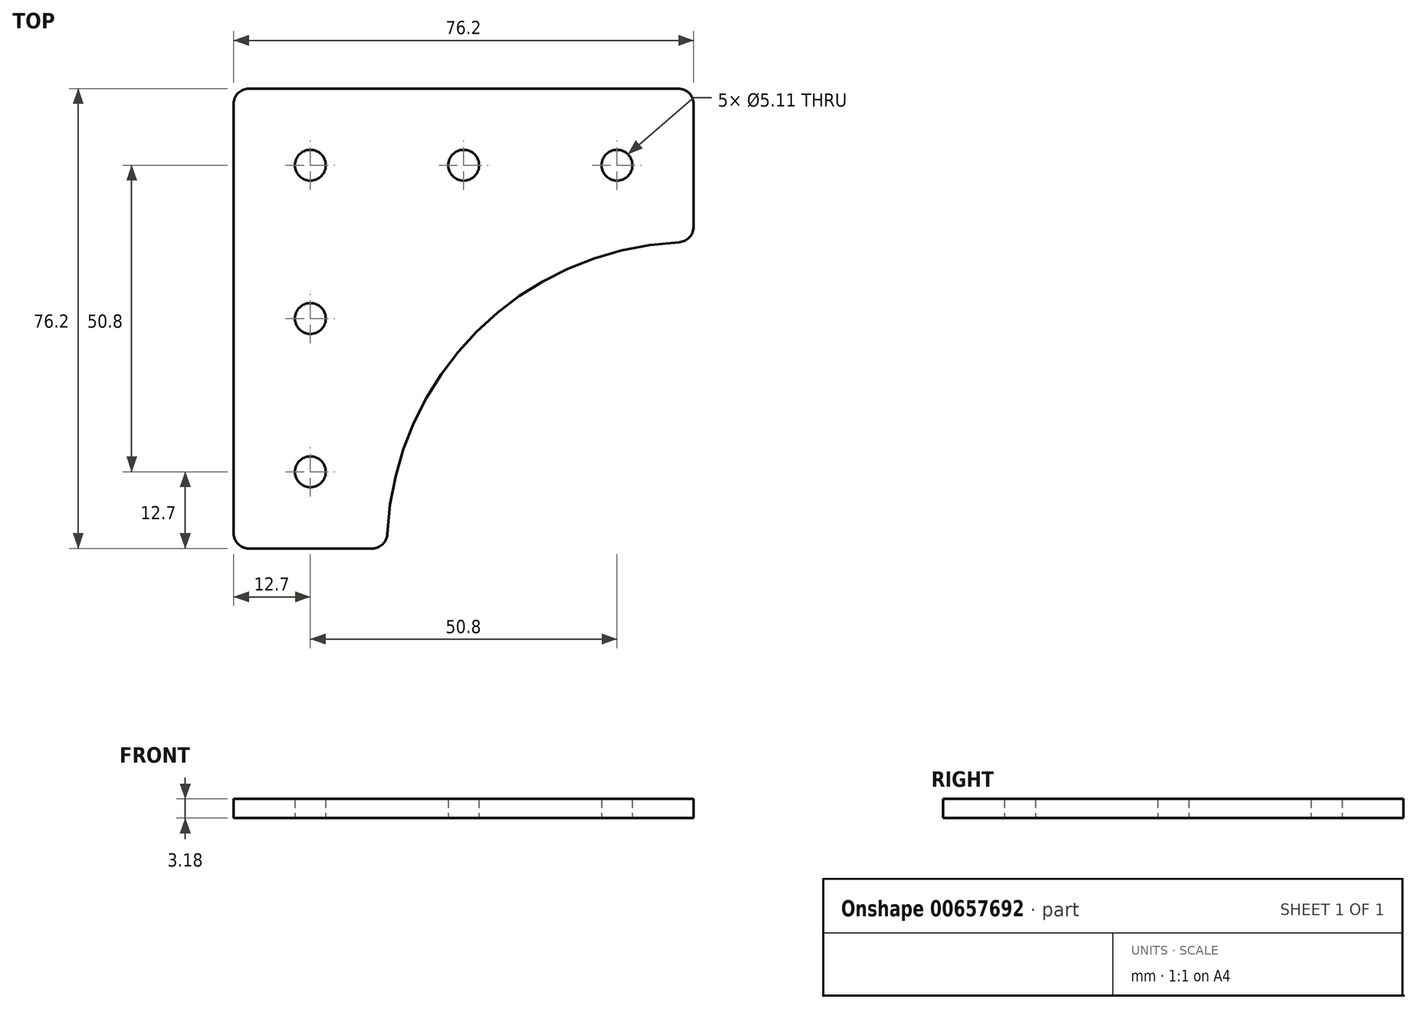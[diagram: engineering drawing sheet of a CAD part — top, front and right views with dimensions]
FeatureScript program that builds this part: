
annotation { "Feature Type Name" : "Feature", "Feature Type Description" : "" }
export const myFeature = defineFeature(function(context is Context, id is Id, definition is map)
    precondition{}
    {
        {
            var Q0;
            Q0=qCreatedBy(makeId("Top.planeOp"),FACE);
            var sketch = newSketch(context, id + "F0", { "sketchPlane" : qUnion([Q0])});
            skLineSegment(sketch, "E0.bottom", {"start": v(0, 0) * mm, "end": v(76.2, 0) * mm});
            skLineSegment(sketch, "E0.top", {"start": v(0, -76.2) * mm, "end": v(76.2, -76.2) * mm});
            skLineSegment(sketch, "E0.left", {"start": v(0, 0) * mm, "end": v(0, -76.2) * mm});
            skLineSegment(sketch, "E0.right", {"start": v(76.2, 0) * mm, "end": v(76.2, -76.2) * mm});
            skLineSegment(sketch, "E1", {"start": v(38.1, -76.2) * mm, "end": v(76.2, -38.1) * mm});
            skLineSegment(sketch, "E2", {"start": v(12.7, -76.2) * mm, "end": v(12.7, 0) * mm});
            skLineSegment(sketch, "E3", {"start": v(0, -12.7) * mm, "end": v(76.2, -12.7) * mm});
            skCircle(sketch, "E4", {"center": v(12.7, -12.7) * mm, "radius": 2.55 * mm});
            skCircle(sketch, "E5", {"center": v(38.1, -12.7) * mm, "radius": 2.55 * mm});
            skCircle(sketch, "E6", {"center": v(63.5, -12.7) * mm, "radius": 2.55 * mm});
            skCircle(sketch, "E7", {"center": v(12.7, -38.1) * mm, "radius": 2.55 * mm});
            skCircle(sketch, "E8", {"center": v(12.7, -63.5) * mm, "radius": 2.55 * mm});
            skLineSegment(sketch, "E9.bottom", {"start": v(76.2, -76.2) * mm, "end": v(25.4, -76.2) * mm});
            skLineSegment(sketch, "E9.top", {"start": v(76.2, -25.4) * mm, "end": v(25.4, -25.4) * mm});
            skLineSegment(sketch, "E9.left", {"start": v(76.2, -76.2) * mm, "end": v(76.2, -25.4) * mm});
            skLineSegment(sketch, "E9.right", {"start": v(25.4, -76.2) * mm, "end": v(25.4, -25.4) * mm});
            skSolve(sketch);
        }
        {
            var Q0;
            {var subQ5=sQuery(id+"F0.wireOp",EDGE,"E0.left");var subQ6=sQuery(id+"F0.wireOp",EDGE,"E0.top");var subQ7=makeQuery(id+"F0.imprint","INTERSECT",VERTEX,{"derivedFrom":[subQ6,subQ5]});Q0=makeQuery(id+"F0.imprint","IMPRINT",FACE,{"disambiguationData":[TD([[makeQuery(id+"F0.imprint","IMPRINT",EDGE,{"disambiguationData":[TD([[subQ7,-1.0]])],"derivedFrom":subQ6}),1.0]])]});}
            var Q1;
            {var subQ1=sQuery(id+"F0.wireOp",EDGE,"E0.left");var subQ6=sQuery(id+"F0.wireOp",EDGE,"E0.bottom");var subQ9=makeQuery(id+"F0.imprint","INTERSECT",VERTEX,{"derivedFrom":[subQ6,subQ1]});Q1=makeQuery(id+"F0.imprint","IMPRINT",FACE,{"disambiguationData":[TD([[makeQuery(id+"F0.imprint","IMPRINT",EDGE,{"disambiguationData":[TD([[subQ9,-1.0]])],"derivedFrom":subQ6}),-1.0]])]});}
            var Q2;
            {var subQ1=sQuery(id+"F0.wireOp",EDGE,"E0.bottom");var subQ5=sQuery(id+"F0.wireOp",EDGE,"E0.right");var subQ6=makeQuery(id+"F0.imprint","INTERSECT",VERTEX,{"derivedFrom":[subQ1,subQ5]});Q2=makeQuery(id+"F0.imprint","IMPRINT",FACE,{"disambiguationData":[TD([[makeQuery(id+"F0.imprint","IMPRINT",EDGE,{"disambiguationData":[TD([[subQ6,1.0]])],"derivedFrom":subQ1}),-1.0]])]});}
            var Q3;
            {var subQ4=sQuery(id+"F0.wireOp",EDGE,"E9.top");Q3=makeQuery(id+"F0.imprint","IMPRINT",FACE,{"disambiguationData":[TD([[makeQuery(id+"F0.imprint","IMPRINT",EDGE,{"derivedFrom":subQ4}),-1.0]])]});}
            extrude(context, id + "F1", {"entities" : qUnion([Q0, Q1, Q2, Q3]), "depth" : 3.17 * mm, "offsetDistance" : 25.4 * mm});
        }
        {
            var Q0;
            Q0=makeQuery(id+"F1.opExtrude","SWEPT_EDGE",EDGE,{"disambiguationData":[OSD([sQuery(id+"F0.wireOp",EDGE,"E9.top"),sQuery(id+"F0.wireOp",EDGE,"E9.right")])]});
            fillet(context, id + "F2", {"entities" : qUnion([Q0]), "tangentPropagation" : true, "radius" : 50.8 * mm, "defaultsChanged" : true, "vertexSettings" : [], "allowEdgeOverflow" : false});
        }
        {
            var Q0;
            Q0=makeQuery(id+"F1.opExtrude","SWEPT_EDGE",EDGE,{"disambiguationData":[OSD([sQuery(id+"F0.wireOp",EDGE,"E0.bottom"),sQuery(id+"F0.wireOp",EDGE,"E0.left")])]});
            var Q1;
            Q1=makeQuery(id+"F1.opExtrude","SWEPT_EDGE",EDGE,{"disambiguationData":[OSD([sQuery(id+"F0.wireOp",EDGE,"E0.top"),sQuery(id+"F0.wireOp",EDGE,"E0.left")])]});
            var Q2;
            Q2=makeQuery(id+"F2.opFillet","BLEND_EDGE",EDGE,{"blendedFrom":[makeQuery(id+"F1.opExtrude","SWEPT_EDGE",EDGE,{"disambiguationData":[OSD([sQuery(id+"F0.wireOp",EDGE,"E9.top"),sQuery(id+"F0.wireOp",EDGE,"E9.right")])]}),makeQuery(id+"F1.opExtrude","SWEPT_FACE",FACE,{"disambiguationData":[OSD([sQuery(id+"F0.wireOp",EDGE,"E0.top")])]})],"blendedInto":[makeQuery(id+"F1.opExtrude","SWEPT_FACE",FACE,{"disambiguationData":[OSD([sQuery(id+"F0.wireOp",EDGE,"E0.top")])]})]});
            var Q3;
            Q3=makeQuery(id+"F1.opExtrude","SWEPT_EDGE",EDGE,{"disambiguationData":[OSD([sQuery(id+"F0.wireOp",EDGE,"E0.bottom"),sQuery(id+"F0.wireOp",EDGE,"E0.right")])]});
            var Q4;
            Q4=makeQuery(id+"F2.opFillet","BLEND_EDGE",EDGE,{"blendedFrom":[makeQuery(id+"F1.opExtrude","SWEPT_EDGE",EDGE,{"disambiguationData":[OSD([sQuery(id+"F0.wireOp",EDGE,"E9.top"),sQuery(id+"F0.wireOp",EDGE,"E9.right")])]}),makeQuery(id+"F1.opExtrude","SWEPT_FACE",FACE,{"disambiguationData":[OSD([sQuery(id+"F0.wireOp",EDGE,"E0.right")])]})],"blendedInto":[makeQuery(id+"F1.opExtrude","SWEPT_FACE",FACE,{"disambiguationData":[OSD([sQuery(id+"F0.wireOp",EDGE,"E0.right")])]})]});
            fillet(context, id + "F3", {"entities" : qUnion([Q0, Q1, Q2, Q3, Q4]), "tangentPropagation" : true, "radius" : 2.54 * mm, "defaultsChanged" : false, "vertexSettings" : [], "allowEdgeOverflow" : false});
        }
    });
